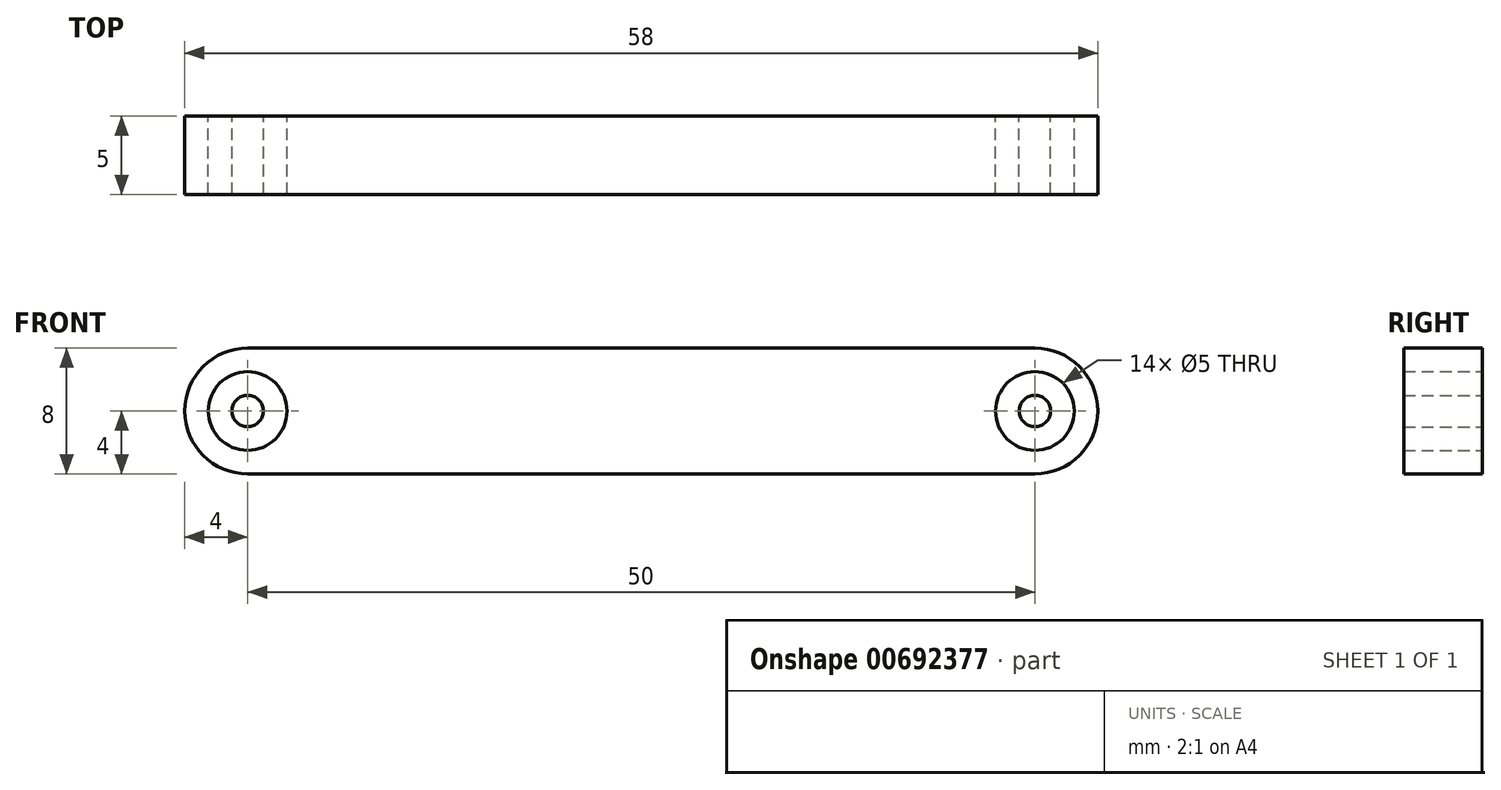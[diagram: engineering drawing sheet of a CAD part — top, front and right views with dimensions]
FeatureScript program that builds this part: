
annotation { "Feature Type Name" : "Feature", "Feature Type Description" : "" }
export const myFeature = defineFeature(function(context is Context, id is Id, definition is map)
    precondition{}
    {
        {
            var Q0;
            Q0=qCreatedBy(makeId("Front.planeOp"),FACE);
            var sketch = newSketch(context, id + "F0", { "sketchPlane" : qUnion([Q0])});
            skArc(sketch, "E0", {"start": v(0, 4) * mm, "mid": v(-4, 0) * mm, "end": v(0, -4) * mm});
            skArc(sketch, "E1", {"start": v(50, -4) * mm, "mid": v(54, 0) * mm, "end": v(50, 4) * mm});
            skLineSegment(sketch, "E2", {"start": v(0, 4) * mm, "end": v(50, 4) * mm});
            skLineSegment(sketch, "E3", {"start": v(0, -4) * mm, "end": v(50, -4) * mm});
            skCircle(sketch, "E4", {"center": v(0, 0) * mm, "radius": 2.5 * mm});
            skCircle(sketch, "E5", {"center": v(0, 0) * mm, "radius": 1 * mm});
            skCircle(sketch, "E6", {"center": v(50, 0) * mm, "radius": 2.5 * mm});
            skCircle(sketch, "E7", {"center": v(50, 0) * mm, "radius": 1 * mm});
            skSolve(sketch);
        }
        {
            var Q0;
            Q0 = qSketchRegion(id + "F0", true);
            var Q1;
            Q1=makeQuery(id+"F0.imprint","IMPRINT",FACE,{"disambiguationData":[TD([[makeQuery(id+"F0.imprint","IMPRINT",EDGE,{"derivedFrom":sQuery(id+"F0.wireOp",EDGE,"E5")}),1.0]])]});
            var Q2;
            Q2=makeQuery(id+"F0.imprint","IMPRINT",FACE,{"disambiguationData":[TD([[makeQuery(id+"F0.imprint","IMPRINT",EDGE,{"derivedFrom":sQuery(id+"F0.wireOp",EDGE,"E7")}),1.0]])]});
            extrude(context, id + "F1", {"entities" : qUnion([Q0, Q1, Q2]), "depth" : 5 * mm, "offsetDistance" : 25 * mm});
        }
    });
